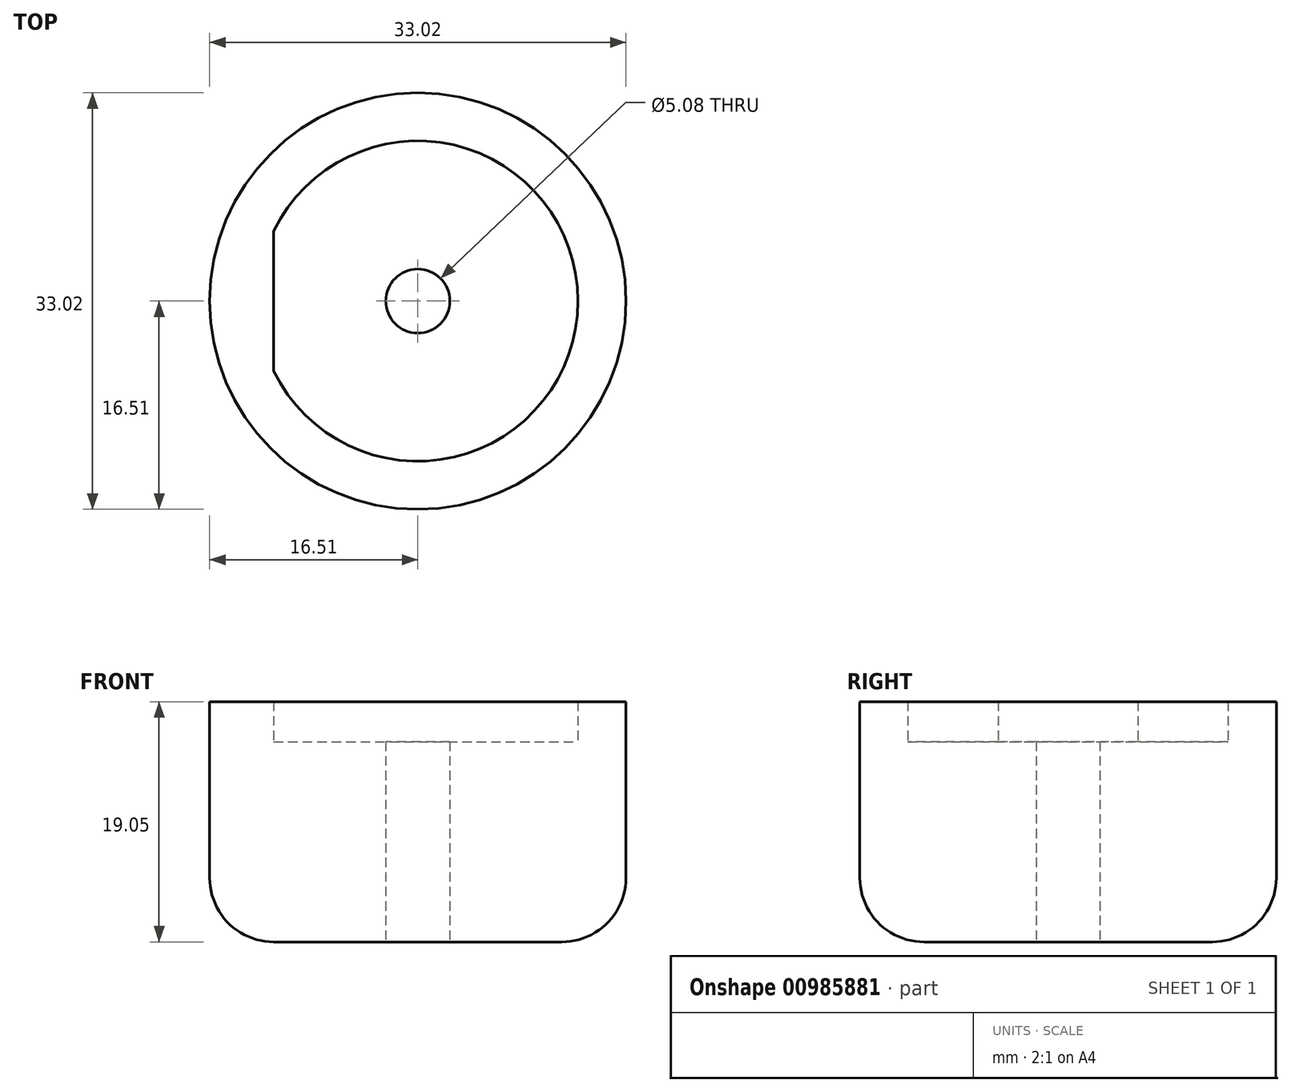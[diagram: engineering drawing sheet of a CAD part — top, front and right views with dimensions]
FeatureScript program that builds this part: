
annotation { "Feature Type Name" : "Feature", "Feature Type Description" : "" }
export const myFeature = defineFeature(function(context is Context, id is Id, definition is map)
    precondition{}
    {
        {
            var Q0;
            Q0=qCreatedBy(makeId("Top.planeOp"),FACE);
            var sketch = newSketch(context, id + "F0", { "sketchPlane" : qUnion([Q0])});
            skCircle(sketch, "E0", {"center": v(0, 0) * mm, "radius": 12.7 * mm});
            skCircle(sketch, "E1", {"center": v(0, 0) * mm, "radius": 16.51 * mm});
            skSolve(sketch);
        }
        {
            var Q0;
            Q0=makeQuery(id+"F0.imprint","IMPRINT",FACE,{"disambiguationData":[TD([[makeQuery(id+"F0.imprint","IMPRINT",EDGE,{"derivedFrom":sQuery(id+"F0.wireOp",EDGE,"E0")}),1.0]])]});
            extrude(context, id + "F1", {"entities" : qUnion([Q0]), "depth" : 15.88 * mm, "offsetDistance" : 25.4 * mm});
        }
        {
            var Q0;
            Q0=makeQuery(id+"F0.imprint","IMPRINT",FACE,{"disambiguationData":[TD([[makeQuery(id+"F0.imprint","IMPRINT",EDGE,{"derivedFrom":sQuery(id+"F0.wireOp",EDGE,"E0")}),-1.0]])]});
            extrude(context, id + "F2", {"entities" : qUnion([Q0]), "operationType" : NewBodyOperationType.ADD, "depth" : 19.05 * mm, "offsetDistance" : 25.4 * mm});
        }
        {
            var Q0;
            Q0=makeQuery(id+"F1.opExtrude","CAP_FACE",FACE,{"disambiguationData":[OSD([sQuery(id+"F0.wireOp",EDGE,"E0")])],"isStart":false});
            var sketch = newSketch(context, id + "F3", { "sketchPlane" : qUnion([Q0])});
            skLineSegment(sketch, "E2", {"start": v(-11.43, 5.54) * mm, "end": v(-11.43, -5.54) * mm});
            skSolve(sketch);
        }
        {
            var Q0;
            {var subQ0=sQuery(id+"F3.wireOp",EDGE,"E2");Q0=makeQuery(id+"F3.imprint","IMPRINT",FACE,{"disambiguationData":[TD([[makeQuery(id+"F3.imprint","IMPRINT",EDGE,{"derivedFrom":subQ0}),-1.0]])]});}
            var Q1;
            Q1=makeQuery(id+"F2.opExtrude","CAP_FACE",FACE,{"disambiguationData":[OSD([sQuery(id+"F0.wireOp",EDGE,"E0"),sQuery(id+"F0.wireOp",EDGE,"E1")])],"isStart":false});
            extrude(context, id + "F4", {"entities" : qUnion([Q0]), "operationType" : NewBodyOperationType.ADD, "endBound" : BoundingType.UP_TO_SURFACE, "depth" : 25.4 * mm, "endBoundEntityFace" : qUnion([Q1]), "offsetDistance" : 25.4 * mm});
        }
        {
            var Q0;
            {var subQ0=sQuery(id+"F0.wireOp",EDGE,"E0");Q0=makeQuery(id+"F2.boolean.opBoolean","MERGE",FACE,{"derivedFrom":[makeQuery(id+"F1.opExtrude","CAP_FACE",FACE,{"disambiguationData":[OSD([subQ0])],"isStart":true}),makeQuery(id+"F2.opExtrude","CAP_FACE",FACE,{"disambiguationData":[OSD([subQ0,sQuery(id+"F0.wireOp",EDGE,"E1")])],"isStart":true})]});}
            var sketch = newSketch(context, id + "F5", { "sketchPlane" : qUnion([Q0])});
            skCircle(sketch, "E3", {"center": v(0, 0) * mm, "radius": 2.54 * mm});
            skSolve(sketch);
        }
        {
            var Q0;
            Q0=makeQuery(id+"F5.imprint","IMPRINT",FACE,{"disambiguationData":[TD([[makeQuery(id+"F5.imprint","IMPRINT",EDGE,{"derivedFrom":sQuery(id+"F5.wireOp",EDGE,"E3")}),1.0]])]});
            extrude(context, id + "F6", {"entities" : qUnion([Q0]), "operationType" : NewBodyOperationType.REMOVE, "endBound" : BoundingType.THROUGH_ALL, "oppositeDirection" : true, "depth" : 25.4 * mm, "offsetDistance" : 25.4 * mm});
        }
        {
            var Q0;
            Q0=makeQuery(id+"F2.opExtrude","CAP_EDGE",EDGE,{"disambiguationData":[OSD([sQuery(id+"F0.wireOp",EDGE,"E1")])],"isStart":true});
            var Q1;
            Q1=makeQuery(id+"F6.boolean.opBoolean","COPY",EDGE,{"derivedFrom":makeQuery(id+"F6.opExtrude","CAP_EDGE",EDGE,{"disambiguationData":[OSD([sQuery(id+"F5.wireOp",EDGE,"E3")])],"isStart":true})});
            fillet(context, id + "F7", {"entities" : qUnion([Q0, Q1]), "radius" : 5.08 * mm, "tangentPropagation" : true, "allowEdgeOverflow" : false});
        }
    });
